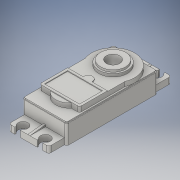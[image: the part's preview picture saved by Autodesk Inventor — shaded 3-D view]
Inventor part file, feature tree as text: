
AUTODESK INVENTOR PART (.ipt)
format: ipt  version: 2021.2 (Build 252289000, 289)  size: 296,960 bytes
history: native  units: mm
features: sketch x13, extrude x12, mirror x2, fillet x2, other x1
ambient origin geometry x8: Origin, YZ Plane, XZ Plane, XY Plane, X Axis, Y Axis, Z Axis, Center Point
bodies: Body1 (feature_tree)
feature tree (30):
  other  "Sólido1"
  extrude  "Extrusión1"  Depth=40.6mm
  extrude  "Extrusión2"  Depth=9.0mm
  extrude  "Extrusión5"  Depth=9.0mm TaperAngle=0.0deg
  extrude  "Extrusión6"  Depth=2.8mm TaperAngle=0.0deg
  extrude  "Extrusión7"  Depth=2.8mm TaperAngle=0.0deg
  mirror  "Simetría3"
  mirror  "Simetría4"
  extrude  "Extrusión8"  Depth=1.0mm TaperAngle=0.0deg
  extrude  "Extrusión9"  Depth=9.6mm
  extrude  "Extrusión10"  Depth=2.0mm TaperAngle=0.0deg
  extrude  "Extrusión11"  Depth=9.4mm
  extrude  "Extrusión12"  Depth=2.0mm
  extrude  "Extrusión13"  Depth=1.3mm
  extrude  "Extrusión14"  Depth=17.8mm
  fillet  "Empalme1"  Radius=12.5mm
  fillet  "Empalme2"  Radius=1.1mm
  sketch  "Boceto18"  dims[d64=0.3mm d65=0.0mm d66=3.88mm d67=1.44mm d68=0.3mm d69=0.0mm d70=0.3mm d71=0.5mm d72=0.0mm d73=1.0mm d74=0.7mm]
  sketch  "Boceto1"  dims[d0=19.8mm d1=40.6mm]
  sketch  "Boceto2"  dims[d2=9.0mm d3=0.0mm d4=6.0mm]
  sketch  "Boceto5"  dims[d5=10.0mm d6=9.0mm d7=0.0mm]
  sketch  "Boceto6"  dims[d23=17.8mm d24=7.0mm d25=2.8mm d26=0.0mm]
  sketch  "Boceto8"  dims[d27=4.4mm d28=2.41mm d29=5.0mm d30=2.65mm d31=0.6mm d32=2.8mm d33=0.0mm]
  sketch  "Boceto9"  dims[d34=0.8mm d35=1.0mm d36=0.0mm]
  sketch  "Boceto11"  dims[d37=19.2mm d40=9.6mm]
  sketch  "Boceto12"  dims[d42=20.3mm d43=2.0mm d44=0.0mm]
  sketch  "Boceto13"  dims[d50=2.2mm d51=9.4mm]
  sketch  "Boceto15"  dims[d52=2.0mm d53=0.0mm d54=12.8mm]
  sketch  "Boceto16"  dims[d55=1.3mm d56=0.0mm d57=11.2mm]
  sketch  "Boceto17"  dims[d58=0.9mm d59=0.0mm d61=17.8mm d62=12.5mm d63=1.1mm]
